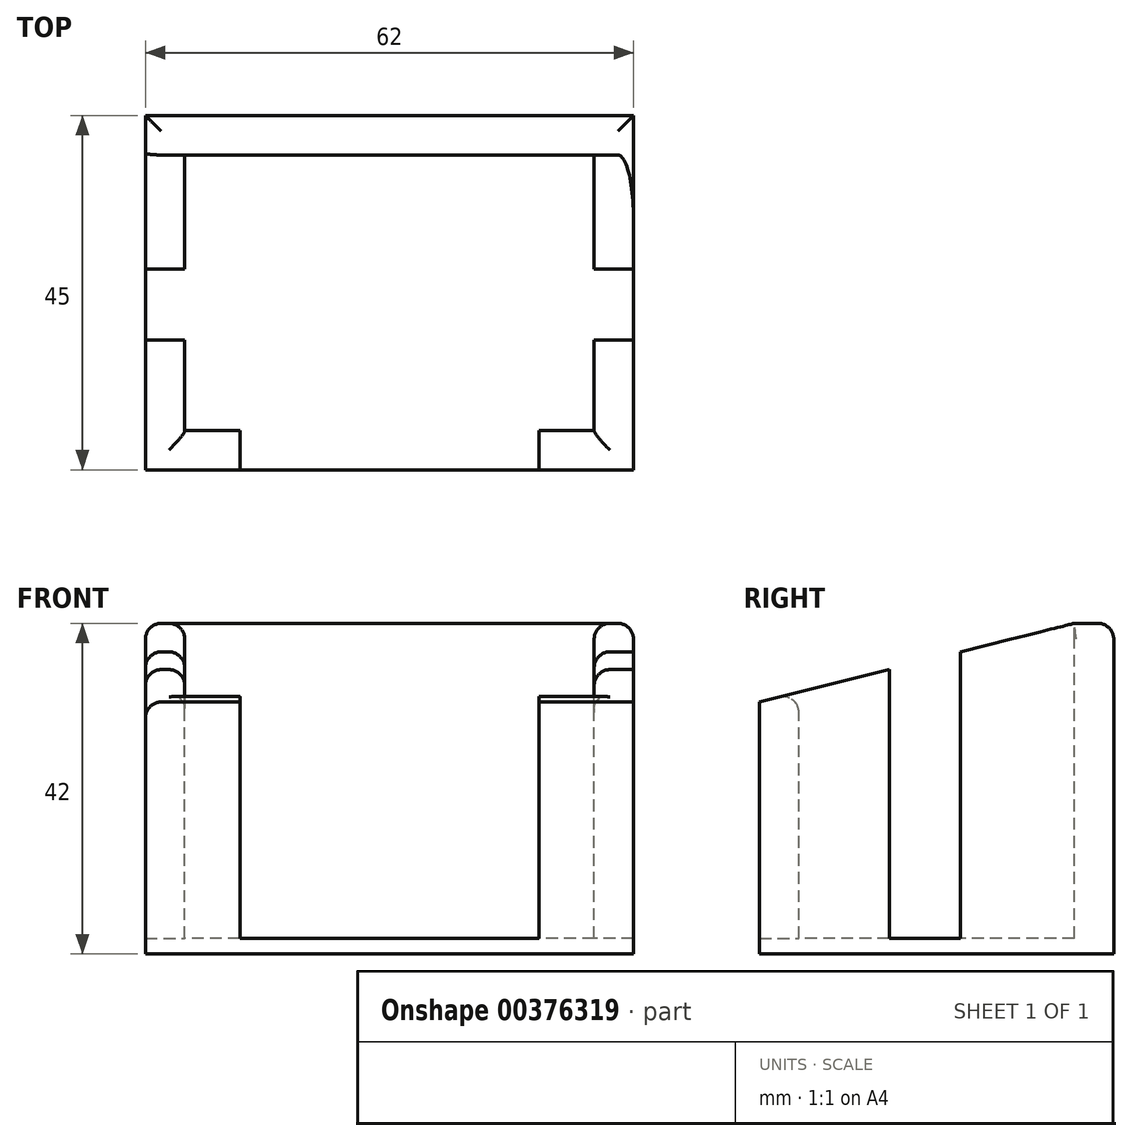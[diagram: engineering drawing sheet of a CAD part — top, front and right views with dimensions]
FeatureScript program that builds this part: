
annotation { "Feature Type Name" : "Feature", "Feature Type Description" : "" }
export const myFeature = defineFeature(function(context is Context, id is Id, definition is map)
    precondition{}
    {
        {
            var Q0;
            Q0=qCreatedBy(makeId("Top.planeOp"),FACE);
            var sketch = newSketch(context, id + "F0", { "sketchPlane" : qUnion([Q0])});
            skLineSegment(sketch, "E0.bottom", {"start": v(-31, 22.5) * mm, "end": v(31, 22.5) * mm});
            skLineSegment(sketch, "E0.top", {"start": v(-31, -22.5) * mm, "end": v(31, -22.5) * mm});
            skLineSegment(sketch, "E0.left", {"start": v(-31, 22.5) * mm, "end": v(-31, -22.5) * mm});
            skLineSegment(sketch, "E0.right", {"start": v(31, 22.5) * mm, "end": v(31, -22.5) * mm});
            skPoint(sketch, "E0.middle", {"position": v(0, 0) * mm});
            skSolve(sketch);
        }
        {
            var Q0;
            Q0 = qSketchRegion(id + "F0", true);
            extrude(context, id + "F1", {"entities" : qUnion([Q0]), "depth" : 42 * mm});
        }
        {
            var Q0;
            Q0=makeQuery(id+"F1.opExtrude","CAP_FACE",FACE,{"disambiguationData":[OSD([sQuery(id+"F0.wireOp",EDGE,"E0.bottom"),sQuery(id+"F0.wireOp",EDGE,"E0.top"),sQuery(id+"F0.wireOp",EDGE,"E0.left"),sQuery(id+"F0.wireOp",EDGE,"E0.right")])],"isStart":false});
            var sketch = newSketch(context, id + "F2", { "sketchPlane" : qUnion([Q0])});
            skLineSegment(sketch, "E1", {"start": v(-19, -22.5) * mm, "end": v(-19, -17.5) * mm});
            skLineSegment(sketch, "E2", {"start": v(-19, -17.5) * mm, "end": v(-26, -17.5) * mm});
            skLineSegment(sketch, "E3", {"start": v(-26, -17.5) * mm, "end": v(-26, -6) * mm});
            skLineSegment(sketch, "E4", {"start": v(-26, -6) * mm, "end": v(-31, -6) * mm});
            skLineSegment(sketch, "E5", {"start": v(-31, -6) * mm, "end": v(-31, 3) * mm});
            skLineSegment(sketch, "E6", {"start": v(-31, 3) * mm, "end": v(-26, 3) * mm});
            skLineSegment(sketch, "E7", {"start": v(-26, 3) * mm, "end": v(-26, 17.5) * mm});
            skLineSegment(sketch, "E8", {"start": v(-26, 17.5) * mm, "end": v(26, 17.5) * mm});
            skLineSegment(sketch, "E9", {"start": v(26, 17.5) * mm, "end": v(26, 3) * mm});
            skLineSegment(sketch, "E10", {"start": v(26, 3) * mm, "end": v(31, 3) * mm});
            skLineSegment(sketch, "E11", {"start": v(31, 3) * mm, "end": v(31, -6) * mm});
            skLineSegment(sketch, "E12", {"start": v(31, -6) * mm, "end": v(26, -6) * mm});
            skLineSegment(sketch, "E13", {"start": v(26, -6) * mm, "end": v(26, -17.5) * mm});
            skLineSegment(sketch, "E14", {"start": v(26, -17.5) * mm, "end": v(19, -17.5) * mm});
            skLineSegment(sketch, "E15", {"start": v(19, -17.5) * mm, "end": v(19, -22.5) * mm});
            skLineSegment(sketch, "E16", {"start": v(19, -22.5) * mm, "end": v(-19, -22.5) * mm});
            skSolve(sketch);
        }
        {
            var Q0;
            Q0 = qSketchRegion(id + "F2", true);
            extrude(context, id + "F3", {"entities" : qUnion([Q0]), "operationType" : NewBodyOperationType.REMOVE, "oppositeDirection" : true, "depth" : 40 * mm});
        }
        {
            var Q0;
            Q0=makeQuery(id+"F1.opExtrude","SWEPT_FACE",FACE,{"disambiguationData":[OSD([sQuery(id+"F0.wireOp",EDGE,"E0.right")])]});
            var sketch = newSketch(context, id + "F4", { "sketchPlane" : qUnion([Q0])});
            skLineSegment(sketch, "E17", {"start": v(-22.5, 42) * mm, "end": v(17.5, 42) * mm});
            skLineSegment(sketch, "E18", {"start": v(17.5, 42) * mm, "end": v(-22.5, 32) * mm});
            skLineSegment(sketch, "E19", {"start": v(-22.5, 32) * mm, "end": v(-22.5, 42) * mm});
            skSolve(sketch);
        }
        {
            var Q0;
            Q0 = qSketchRegion(id + "F4", true);
            extrude(context, id + "F5", {"entities" : qUnion([Q0]), "operationType" : NewBodyOperationType.REMOVE, "endBound" : BoundingType.THROUGH_ALL, "oppositeDirection" : true, "depth" : 25 * mm});
        }
        {
            var Q0;
            Q0=makeQuery(id+"F5.boolean.opBoolean","INTERSECT",EDGE,{"derivedFrom":[makeQuery(id+"F3.boolean.opBoolean","COPY",FACE,{"derivedFrom":makeQuery(id+"F3.opExtrude","SWEPT_FACE",FACE,{"disambiguationData":[OSD([sQuery(id+"F2.wireOp",EDGE,"E14")])]})}),makeQuery(id+"F5.opExtrude","SWEPT_FACE",FACE,{"disambiguationData":[OSD([sQuery(id+"F4.wireOp",EDGE,"E18")])]})]});
            var Q1;
            Q1=makeQuery(id+"F5.boolean.opBoolean","INTERSECT",EDGE,{"derivedFrom":[makeQuery(id+"F3.boolean.opBoolean","COPY",FACE,{"derivedFrom":makeQuery(id+"F3.opExtrude","SWEPT_FACE",FACE,{"disambiguationData":[OSD([sQuery(id+"F2.wireOp",EDGE,"E13")])]})}),makeQuery(id+"F5.opExtrude","SWEPT_FACE",FACE,{"disambiguationData":[OSD([sQuery(id+"F4.wireOp",EDGE,"E18")])]})]});
            var Q2;
            {var subQ0=sQuery(id+"F4.wireOp",EDGE,"E18");Q2=makeQuery(id+"F5.boolean.opBoolean","COPY",EDGE,{"disambiguationData":[TD([makeQuery(id+"F1.opExtrude","SWEPT_FACE",FACE,{"disambiguationData":[OSD([sQuery(id+"F0.wireOp",EDGE,"E0.top")])]})])],"derivedFrom":makeQuery(id+"F5.opExtrude","CAP_EDGE",EDGE,{"disambiguationData":[OSD([subQ0])],"isStart":true})});}
            var Q3;
            {var subQ0=sQuery(id+"F0.wireOp",EDGE,"E0.top");var subQ1=sQuery(id+"F0.wireOp",EDGE,"E0.right");var subQ2=sQuery(id+"F4.wireOp",EDGE,"E18");Q3=makeQuery(id+"F5.boolean.opBoolean","COPY",EDGE,{"disambiguationData":[TD([makeQuery(id+"F1.opExtrude","SWEPT_FACE",FACE,{"disambiguationData":[OSD([subQ1])]})])],"derivedFrom":makeQuery(id+"F5.opExtrude","SWEPT_EDGE",EDGE,{"disambiguationData":[OSD([subQ0,subQ1,subQ2,sQuery(id+"F4.wireOp",EDGE,"E19")])]})});}
            var Q4;
            Q4=makeQuery(id+"F5.boolean.opBoolean","INTERSECT",EDGE,{"derivedFrom":[makeQuery(id+"F3.boolean.opBoolean","COPY",FACE,{"derivedFrom":makeQuery(id+"F3.opExtrude","SWEPT_FACE",FACE,{"disambiguationData":[OSD([sQuery(id+"F2.wireOp",EDGE,"E9")])]})}),makeQuery(id+"F5.opExtrude","SWEPT_FACE",FACE,{"disambiguationData":[OSD([sQuery(id+"F4.wireOp",EDGE,"E18")])]})]});
            var Q5;
            Q5=makeQuery(id+"F5.boolean.opBoolean","INTERSECT",EDGE,{"derivedFrom":[makeQuery(id+"F3.boolean.opBoolean","COPY",FACE,{"derivedFrom":makeQuery(id+"F3.opExtrude","SWEPT_FACE",FACE,{"disambiguationData":[OSD([sQuery(id+"F2.wireOp",EDGE,"E7")])]})}),makeQuery(id+"F5.opExtrude","SWEPT_FACE",FACE,{"disambiguationData":[OSD([sQuery(id+"F4.wireOp",EDGE,"E18")])]})]});
            var Q6;
            Q6=makeQuery(id+"F5.boolean.opBoolean","INTERSECT",EDGE,{"disambiguationData":[OD(1.0)],"derivedFrom":[makeQuery(id+"F1.opExtrude","SWEPT_FACE",FACE,{"disambiguationData":[OSD([sQuery(id+"F0.wireOp",EDGE,"E0.left")])]}),makeQuery(id+"F5.opExtrude","SWEPT_FACE",FACE,{"disambiguationData":[OSD([sQuery(id+"F4.wireOp",EDGE,"E18")])]})]});
            var Q7;
            Q7=makeQuery(id+"F5.boolean.opBoolean","INTERSECT",EDGE,{"disambiguationData":[OD(0.0)],"derivedFrom":[makeQuery(id+"F1.opExtrude","SWEPT_FACE",FACE,{"disambiguationData":[OSD([sQuery(id+"F0.wireOp",EDGE,"E0.left")])]}),makeQuery(id+"F5.opExtrude","SWEPT_FACE",FACE,{"disambiguationData":[OSD([sQuery(id+"F4.wireOp",EDGE,"E18")])]})]});
            var Q8;
            Q8=makeQuery(id+"F5.boolean.opBoolean","INTERSECT",EDGE,{"derivedFrom":[makeQuery(id+"F3.boolean.opBoolean","COPY",FACE,{"derivedFrom":makeQuery(id+"F3.opExtrude","SWEPT_FACE",FACE,{"disambiguationData":[OSD([sQuery(id+"F2.wireOp",EDGE,"E3")])]})}),makeQuery(id+"F5.opExtrude","SWEPT_FACE",FACE,{"disambiguationData":[OSD([sQuery(id+"F4.wireOp",EDGE,"E18")])]})]});
            var Q9;
            Q9=makeQuery(id+"F5.boolean.opBoolean","INTERSECT",EDGE,{"derivedFrom":[makeQuery(id+"F3.boolean.opBoolean","COPY",FACE,{"derivedFrom":makeQuery(id+"F3.opExtrude","SWEPT_FACE",FACE,{"disambiguationData":[OSD([sQuery(id+"F2.wireOp",EDGE,"E2")])]})}),makeQuery(id+"F5.opExtrude","SWEPT_FACE",FACE,{"disambiguationData":[OSD([sQuery(id+"F4.wireOp",EDGE,"E18")])]})]});
            var Q10;
            {var subQ0=sQuery(id+"F0.wireOp",EDGE,"E0.top");var subQ1=sQuery(id+"F4.wireOp",EDGE,"E18");Q10=makeQuery(id+"F5.boolean.opBoolean","COPY",EDGE,{"disambiguationData":[TD([makeQuery(id+"F1.opExtrude","SWEPT_FACE",FACE,{"disambiguationData":[OSD([sQuery(id+"F0.wireOp",EDGE,"E0.left")])]})])],"derivedFrom":makeQuery(id+"F5.opExtrude","SWEPT_EDGE",EDGE,{"disambiguationData":[OSD([subQ0,sQuery(id+"F0.wireOp",EDGE,"E0.right"),subQ1,sQuery(id+"F4.wireOp",EDGE,"E19")])]})});}
            var Q11;
            {var subQ1=sQuery(id+"F4.wireOp",EDGE,"E18");Q11=makeQuery(id+"F5.boolean.opBoolean","COPY",EDGE,{"disambiguationData":[TD([makeQuery(id+"F3.boolean.opBoolean","COPY",FACE,{"derivedFrom":makeQuery(id+"F3.opExtrude","SWEPT_FACE",FACE,{"disambiguationData":[OSD([sQuery(id+"F2.wireOp",EDGE,"E10")])]})})])],"derivedFrom":makeQuery(id+"F5.opExtrude","CAP_EDGE",EDGE,{"disambiguationData":[OSD([subQ1])],"isStart":true})});}
            var Q12;
            {var subQ0=sQuery(id+"F0.wireOp",EDGE,"E0.bottom");var subQ1=sQuery(id+"F0.wireOp",EDGE,"E0.right");Q12=makeQuery(id+"F3.boolean.opBoolean","SPLIT",EDGE,{"disambiguationData":[TD([makeQuery(id+"F1.opExtrude","SWEPT_FACE",FACE,{"disambiguationData":[OSD([subQ0])]})])],"derivedFrom":makeQuery(id+"F1.opExtrude","CAP_EDGE",EDGE,{"disambiguationData":[OSD([subQ1])],"isStart":false})});}
            var Q13;
            Q13=makeQuery(id+"F1.opExtrude","CAP_EDGE",EDGE,{"disambiguationData":[OSD([sQuery(id+"F0.wireOp",EDGE,"E0.bottom")])],"isStart":false});
            var Q14;
            {var subQ0=sQuery(id+"F0.wireOp",EDGE,"E0.bottom");var subQ1=sQuery(id+"F0.wireOp",EDGE,"E0.left");Q14=makeQuery(id+"F3.boolean.opBoolean","SPLIT",EDGE,{"disambiguationData":[TD([makeQuery(id+"F1.opExtrude","SWEPT_FACE",FACE,{"disambiguationData":[OSD([subQ0])]})])],"derivedFrom":makeQuery(id+"F1.opExtrude","CAP_EDGE",EDGE,{"disambiguationData":[OSD([subQ1])],"isStart":false})});}
            fillet(context, id + "F6", {"entities" : qUnion([Q0, Q1, Q2, Q3, Q4, Q5, Q6, Q7, Q8, Q9, Q10, Q11, Q12, Q13, Q14]), "radius" : 2 * mm, "tangentPropagation" : true, "allowEdgeOverflow" : false});
        }
    });
